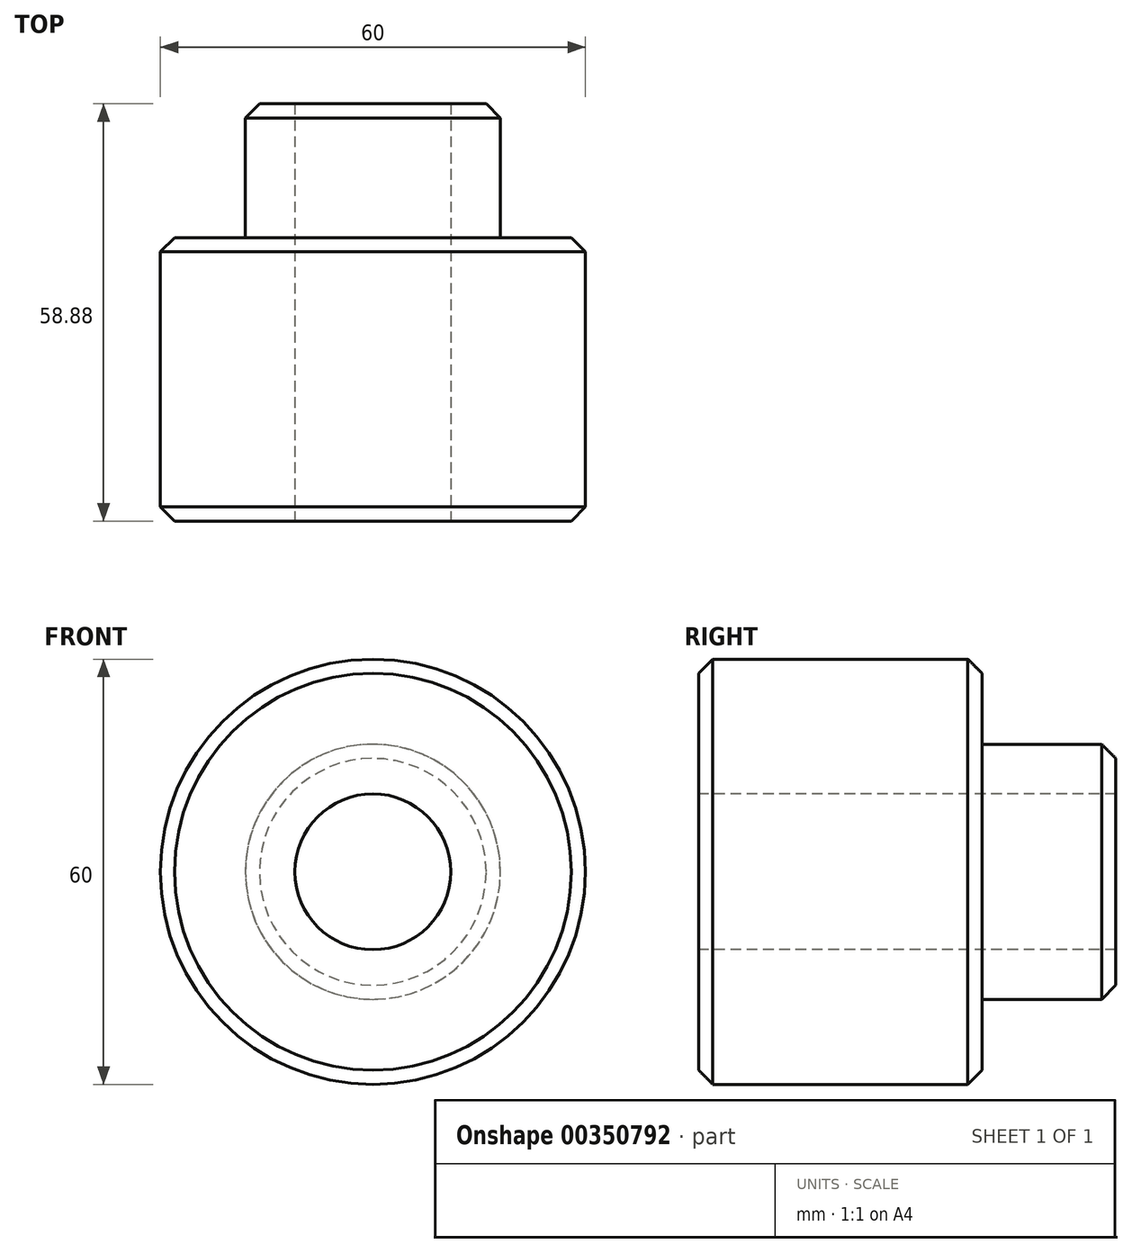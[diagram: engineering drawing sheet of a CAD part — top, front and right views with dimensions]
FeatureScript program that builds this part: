
annotation { "Feature Type Name" : "Feature", "Feature Type Description" : "" }
export const myFeature = defineFeature(function(context is Context, id is Id, definition is map)
    precondition{}
    {
        {
            var Q0;
            Q0=qCreatedBy(makeId("Right.planeOp"),FACE);
            var sketch = newSketch(context, id + "F0", { "sketchPlane" : qUnion([Q0])});
            skLineSegment(sketch, "E0", {"start": v(-55.71, 0) * mm, "end": v(50.63, 0) * mm, "construction": true});
            skLineSegment(sketch, "E1", {"start": v(-24.44, 30) * mm, "end": v(15.56, 30) * mm});
            skLineSegment(sketch, "E2", {"start": v(15.56, 30) * mm, "end": v(15.56, 18) * mm});
            skLineSegment(sketch, "E3", {"start": v(15.56, 18) * mm, "end": v(34.44, 18) * mm});
            skLineSegment(sketch, "E4", {"start": v(34.44, 18) * mm, "end": v(34.44, 11) * mm});
            skLineSegment(sketch, "E5", {"start": v(34.44, 11) * mm, "end": v(-24.44, 11) * mm});
            skLineSegment(sketch, "E6", {"start": v(-24.44, 11) * mm, "end": v(-24.44, 30) * mm});
            skSolve(sketch);
        }
        {
            var Q0;
            Q0 = qSketchRegion(id + "F0", true);
            var Q1;
            Q1=sQuery(id+"F0.wireOp",EDGE,"E0");
            revolve(context, id + "F1", {"entities" : qUnion([Q0]), "axis" : qUnion([Q1]), "revolveType" : RevolveType.FULL});
        }
        {
            var Q0;
            Q0=makeQuery(id+"F1.opRevolve","SWEPT_EDGE",EDGE,{"disambiguationData":[OSD([sQuery(id+"F0.wireOp",EDGE,"E3"),sQuery(id+"F0.wireOp",EDGE,"E4")])]});
            var Q1;
            Q1=makeQuery(id+"F1.opRevolve","SWEPT_EDGE",EDGE,{"disambiguationData":[OSD([sQuery(id+"F0.wireOp",EDGE,"E1"),sQuery(id+"F0.wireOp",EDGE,"E2")])]});
            var Q2;
            Q2=makeQuery(id+"F1.opRevolve","SWEPT_EDGE",EDGE,{"disambiguationData":[OSD([sQuery(id+"F0.wireOp",EDGE,"E1"),sQuery(id+"F0.wireOp",EDGE,"E6")])]});
            chamfer(context, id + "F2", {"entities" : qUnion([Q0, Q1, Q2]), "width" : 2 * mm, "tangentPropagation" : true});
        }
    });
